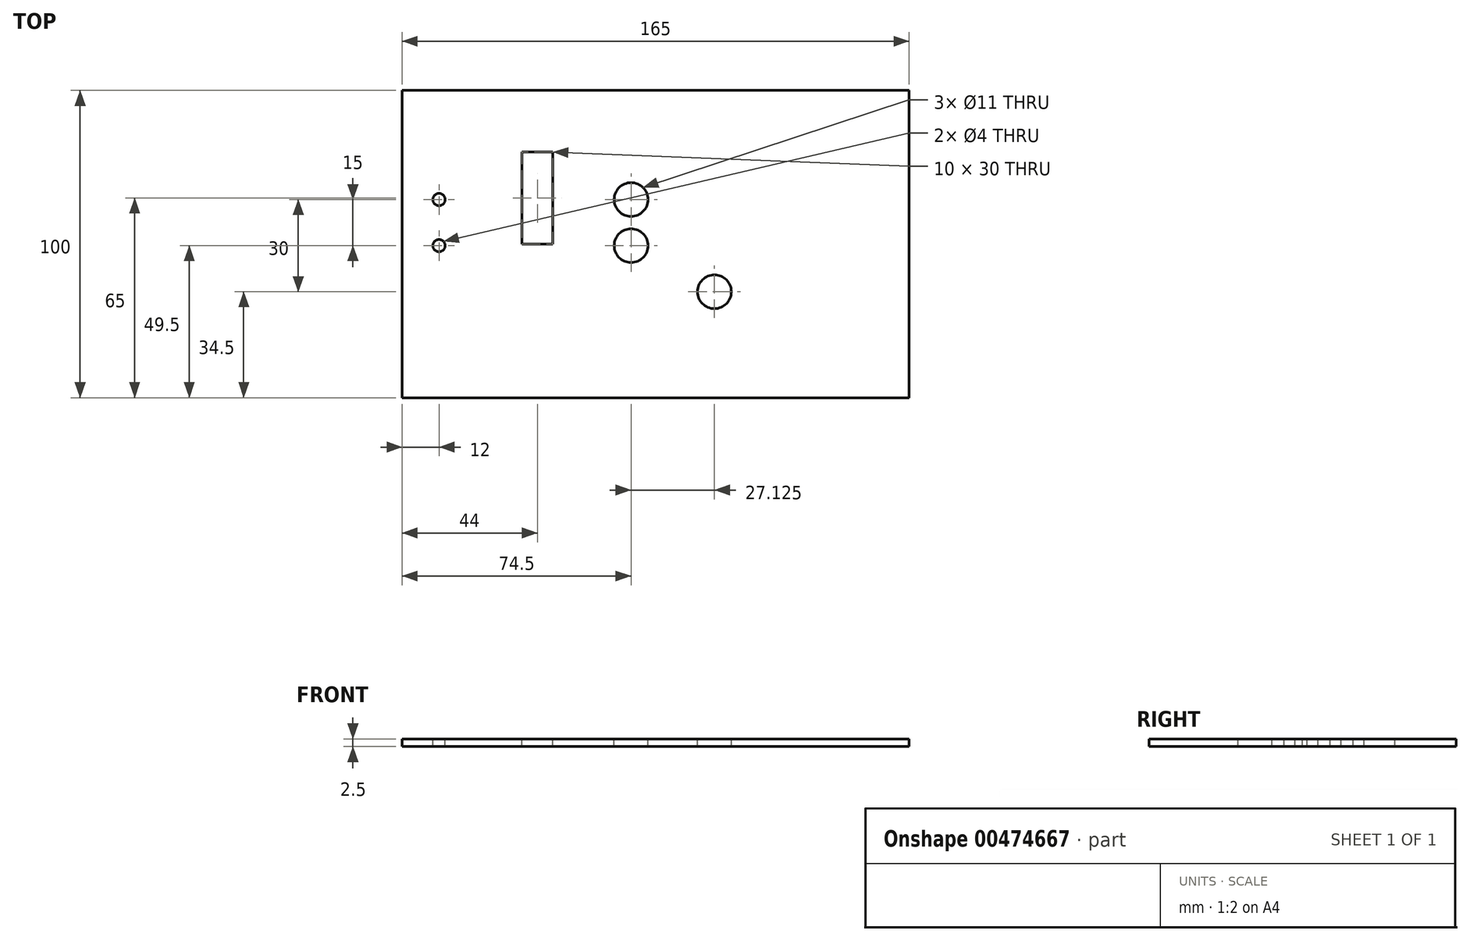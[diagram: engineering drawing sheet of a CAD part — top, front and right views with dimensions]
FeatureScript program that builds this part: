
annotation { "Feature Type Name" : "Feature", "Feature Type Description" : "" }
export const myFeature = defineFeature(function(context is Context, id is Id, definition is map)
    precondition{}
    {
        {
            var Q0;
            Q0=qCreatedBy(makeId("Top.planeOp"),FACE);
            var sketch = newSketch(context, id + "F0", { "sketchPlane" : qUnion([Q0])});
            skLineSegment(sketch, "E0.bottom", {"start": v(-82.5, 50) * mm, "end": v(82.5, 50) * mm});
            skLineSegment(sketch, "E0.top", {"start": v(-82.5, -50) * mm, "end": v(82.5, -50) * mm});
            skLineSegment(sketch, "E0.left", {"start": v(-82.5, 50) * mm, "end": v(-82.5, -50) * mm});
            skLineSegment(sketch, "E0.right", {"start": v(82.5, 50) * mm, "end": v(82.5, -50) * mm});
            skPoint(sketch, "E0.middle", {"position": v(0, 0) * mm});
            skSolve(sketch);
        }
        {
            var Q0;
            Q0 = qSketchRegion(id + "F0", true);
            extrude(context, id + "F1", {"entities" : qUnion([Q0]), "depth" : 2.5 * mm});
        }
        {
            var Q0;
            Q0=makeQuery(id+"F1.opExtrude","CAP_FACE",FACE,{"disambiguationData":[OSD([sQuery(id+"F0.wireOp",EDGE,"E0.bottom"),sQuery(id+"F0.wireOp",EDGE,"E0.top"),sQuery(id+"F0.wireOp",EDGE,"E0.left"),sQuery(id+"F0.wireOp",EDGE,"E0.right")])],"isStart":false});
            var sketch = newSketch(context, id + "F2", { "sketchPlane" : qUnion([Q0])});
            skCircle(sketch, "E1", {"center": v(-8, 14.5) * mm, "radius": 5.5 * mm});
            skCircle(sketch, "E2", {"center": v(-8, -0.5) * mm, "radius": 5.5 * mm});
            skCircle(sketch, "E3", {"center": v(19.13, -15.5) * mm, "radius": 5.5 * mm});
            skLineSegment(sketch, "E4.bottom", {"start": v(-33.5, 0) * mm, "end": v(-43.5, 0) * mm});
            skLineSegment(sketch, "E4.top", {"start": v(-33.5, 30) * mm, "end": v(-43.5, 30) * mm});
            skLineSegment(sketch, "E4.left", {"start": v(-33.5, 0) * mm, "end": v(-33.5, 30) * mm});
            skLineSegment(sketch, "E4.right", {"start": v(-43.5, 0) * mm, "end": v(-43.5, 30) * mm});
            skPoint(sketch, "E4.middle", {"position": v(-38.5, 15) * mm});
            skCircle(sketch, "E5", {"center": v(-70.5, 14.5) * mm, "radius": 2 * mm});
            skCircle(sketch, "E6", {"center": v(-70.5, -0.5) * mm, "radius": 2 * mm});
            skSolve(sketch);
        }
        {
            var Q0;
            Q0 = qSketchRegion(id + "F2", true);
            extrude(context, id + "F3", {"entities" : qUnion([Q0]), "operationType" : NewBodyOperationType.REMOVE, "oppositeDirection" : true, "depth" : 25 * mm});
        }
    });
